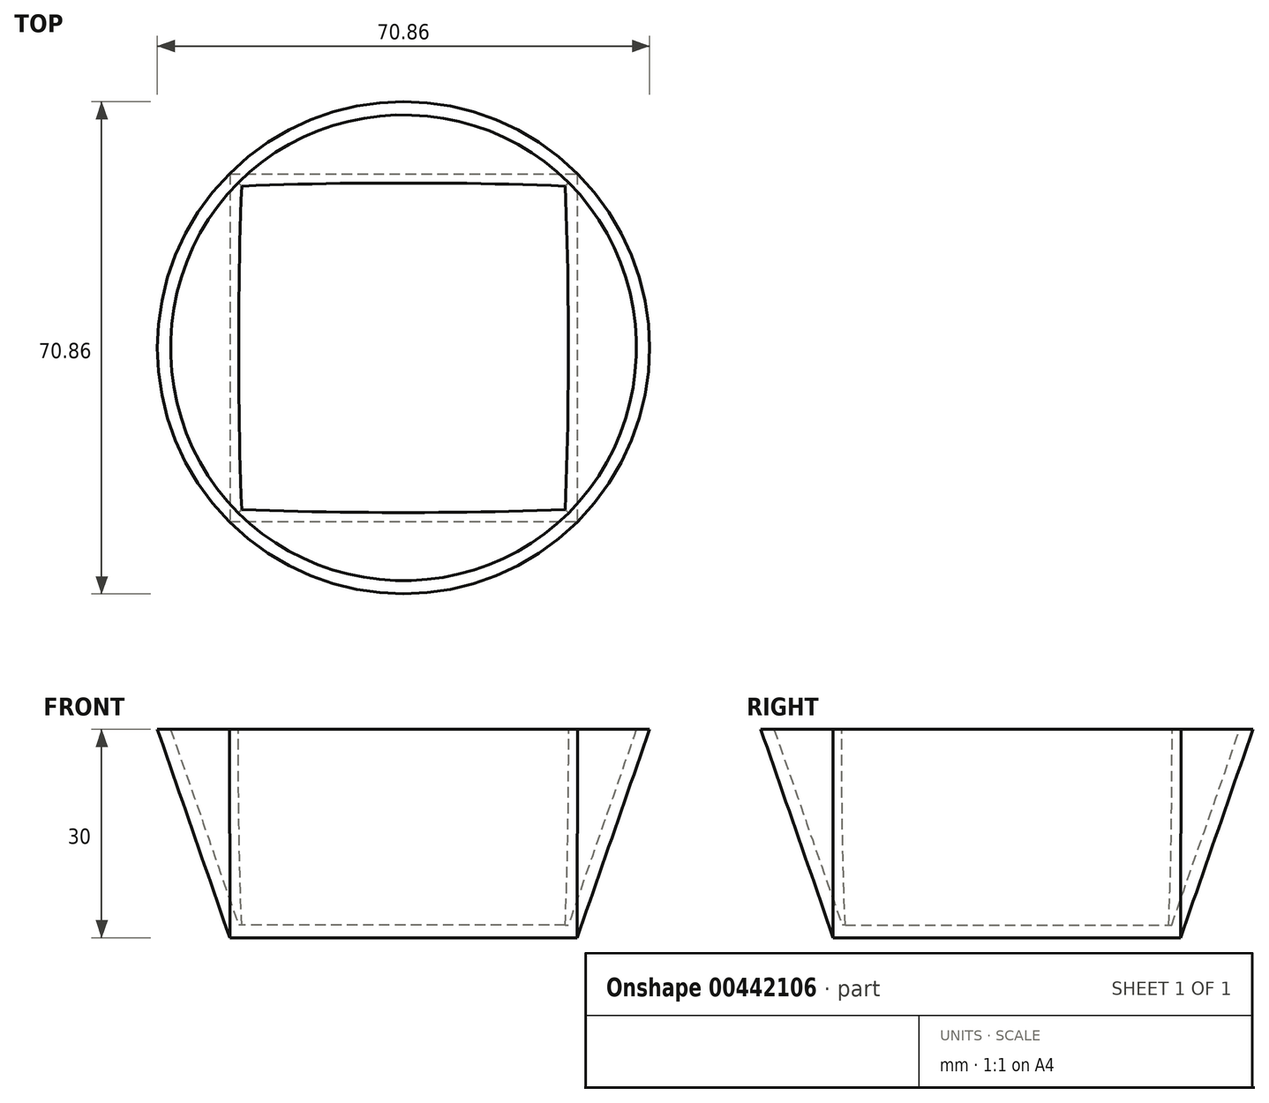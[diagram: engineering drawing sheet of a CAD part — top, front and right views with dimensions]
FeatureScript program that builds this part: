
annotation { "Feature Type Name" : "Feature", "Feature Type Description" : "" }
export const myFeature = defineFeature(function(context is Context, id is Id, definition is map)
    precondition{}
    {
        {
            var Q0;
            Q0=qCreatedBy(makeId("Top.planeOp"),FACE);
            var sketch = newSketch(context, id + "F0", { "sketchPlane" : qUnion([Q0])});
            skLineSegment(sketch, "E0.bottom", {"start": v(-25, 25) * mm, "end": v(25, 25) * mm});
            skLineSegment(sketch, "E0.top", {"start": v(-25, -25) * mm, "end": v(25, -25) * mm});
            skLineSegment(sketch, "E0.left", {"start": v(-25, 25) * mm, "end": v(-25, -25) * mm});
            skLineSegment(sketch, "E0.right", {"start": v(25, 25) * mm, "end": v(25, -25) * mm});
            skPoint(sketch, "E0.middle", {"position": v(0, 0) * mm});
            skSolve(sketch);
        }
        {
            var Q0;
            Q0=qCreatedBy(makeId("Top.planeOp"),FACE);
            cPlane(context, id + "F1", {"entities" : qUnion([Q0]), "cplaneType" : CPlaneType.OFFSET, "offset" : 30 * mm, "width" : 150 * mm, "height" : 150 * mm});
        }
        {
            var Q0;
            Q0=qCreatedBy(id+"F1.planeOp",FACE);
            var sketch = newSketch(context, id + "F2", { "sketchPlane" : qUnion([Q0])});
            skCircle(sketch, "E1", {"center": v(0, 0) * mm, "radius": 35.43 * mm});
            skSolve(sketch);
        }
        {
            var Q0;
            Q0=makeQuery(id+"F0.imprint","IMPRINT",FACE,{"disambiguationData":[TD([[makeQuery(id+"F0.imprint","IMPRINT",EDGE,{"derivedFrom":sQuery(id+"F0.wireOp",EDGE,"E0.bottom")}),-1.0]])]});
            var Q1;
            Q1=makeQuery(id+"F2.imprint","IMPRINT",FACE,{"disambiguationData":[TD([[makeQuery(id+"F2.imprint","IMPRINT",EDGE,{"derivedFrom":sQuery(id+"F2.wireOp",EDGE,"E1")}),1.0]])]});
            loft(context, id + "F3", {"sheetProfilesArray" : [{ "sheetProfileEntities" : qUnion([Q0]) }, { "sheetProfileEntities" : qUnion([Q1]) }]});
        }
        {
            var Q0;
            Q0=makeQuery(id+"F3.opLoft","CAP_FACE",FACE,{"disambiguationData":[OSD([makeQuery(id+"F2.imprint","IMPRINT",FACE,{"disambiguationData":[TD([[makeQuery(id+"F2.imprint","IMPRINT",EDGE,{"derivedFrom":sQuery(id+"F2.wireOp",EDGE,"E1")}),1.0]])]})])],"isStart":true});
            shell(context, id + "F4", {"entities" : qUnion([Q0]), "thickness" : 1.8 * mm});
        }
    });
